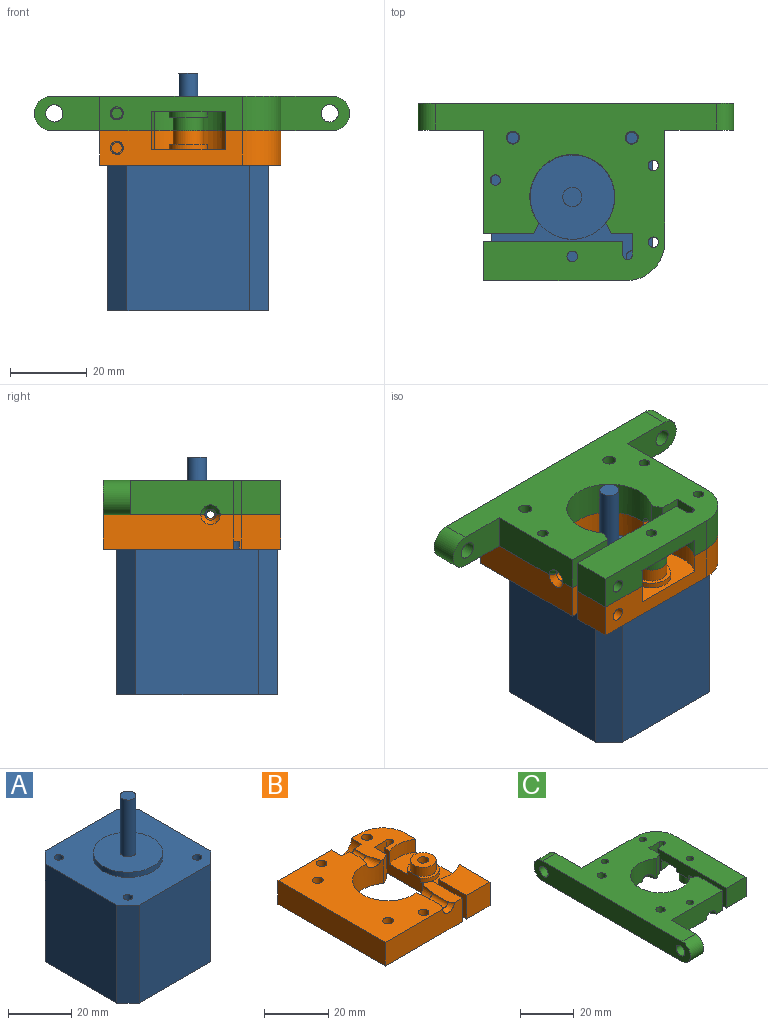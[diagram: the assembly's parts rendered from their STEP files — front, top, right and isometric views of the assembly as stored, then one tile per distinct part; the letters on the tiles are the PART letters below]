
ASSEMBLY  parts=3 mates=1
PART A: 22 faces, bbox 42x42x62 mm
  f0: plane 38x32mm, normal (-1,0,0), area 1216mm2, adj f4,f5,f8,f9
  f1: plane 38x32mm, normal (0,-1,0), area 1216mm2, adj f4,f5,f7,f9
  f2: plane 38x32mm, normal (1,0,0), area 1216mm2, adj f4,f5,f6,f7
  f3: plane 38x32mm, normal (0,1,0), area 1216mm2, adj f4,f5,f6,f8
  f4: plane 42x42mm, normal (0,0,1), area 1305.6mm2, adj f0,f1,f2,f3,f6,f7,f8,f9
  f5: plane 42x42mm, normal (0,0,-1), area 1714mm2, adj f0,f1,f2,f3,f6,f7,f8,f9
  f6: plane 38x5mm, normal (0.71,0.71,0), area 268.7mm2, adj f2,f3,f4,f5
  f7: plane 38x5mm, normal (0.71,-0.71,0), area 268.7mm2, adj f1,f2,f4,f5
  f8: plane 38x5mm, normal (-0.71,0.71,0), area 268.7mm2, adj f0,f3,f4,f5
  f9: plane 38x5mm, normal (-0.71,-0.71,0), area 268.7mm2, adj f0,f1,f4,f5
  f10: cylinder r=11mm len=22mm, axis (0,0,-1), area 138.2mm2, adj f4,f11
  f11: plane 22x22mm, normal (0,0,1), area 360.5mm2, adj f10,f12
  f12: cylinder r=2.5mm len=22mm, axis (0,0,-1), area 345.6mm2, adj f11,f13
  f13: plane 5x5mm, normal (0,0,1), area 19.6mm2, adj f12
  f14: cylinder r=1.5mm len=25mm, axis (0,0,1), area 235.6mm2, adj f4,f15
  f15: plane 3x3mm, normal (0,0,1), area 7.1mm2, adj f14
  f16: cylinder r=1.5mm len=25mm, axis (0,0,1), area 235.6mm2, adj f4,f17
  f17: plane 3x3mm, normal (0,0,1), area 7.1mm2, adj f16
  f18: cylinder r=1.5mm len=25mm, axis (0,0,1), area 235.6mm2, adj f4,f19
  f19: plane 3x3mm, normal (0,0,1), area 7.1mm2, adj f18
  f20: cylinder r=1.5mm len=25mm, axis (0,0,1), area 235.6mm2, adj f4,f21
  f21: plane 3x3mm, normal (0,0,1), area 7.1mm2, adj f20
PART B: 44 faces, bbox 46.2x47.3x9 mm
  f0: plane 47.28x26.93mm, normal (0,0,1), area 962.5mm2, adj f2,f7,f8,f9,f15,f17,f21,f22
  f1: plane 14.38x4.52mm, normal (0,0,1), area 58.8mm2, adj f2,f6,f9,f34,f35,f36,f43
  f2: cylinder r=11.1mm len=22.2mm, axis (0,0,1), area 427.8mm2, adj f0,f1,f3,f20,f29,f33,f34,f42
  f3: plane 17.27x15.32mm, normal (0,0,1), area 163.1mm2, adj f2,f4,f7,f10,f11,f12,f13,f16
  f4: plane 36.35x9mm, normal (-1,0,0), area 219.3mm2, adj f3,f5,f13,f14,f19,f20,f23,f24
  f5: cylinder r=5mm len=10mm, axis (0,0,1), area 37.6mm2, adj f4,f25,f26
  f6: plane 13.04x9mm, normal (1,0,0), area 111.2mm2, adj f1,f9,f20,f38,f43
  f7: plane 36.2x9mm, normal (0,1,0), area 294mm2, adj f0,f3,f8,f20,f30,f37
  f8: plane 47.28x9mm, normal (-1,0,0), area 425.5mm2, adj f0,f7,f9,f20
  f9: plane 33.91x9mm, normal (0,-1,0), area 295mm2, adj f0,f1,f6,f8,f20,f36
  f10: plane 9x5.51mm, normal (1,0,0), area 49.5mm2, adj f3,f11,f20,f42
  f11: plane 9x5.65mm, normal (0,-1,0), area 50.9mm2, adj f3,f10,f12,f20
  f12: cylinder r=1.22mm len=9mm, axis (0,0,-1), area 34.6mm2, adj f3,f11,f13,f20
  f13: plane 9x3.65mm, normal (0,1,0), area 32.9mm2, adj f3,f4,f12,f20
  f14: plane 10.29x9mm, normal (0,-1,0), area 92.6mm2, adj f4,f18,f19,f20
  f15: cylinder r=1.7mm len=9mm, axis (0,0,-1), area 96.1mm2, adj f0,f20
  f16: cylinder r=1.7mm len=9mm, axis (0,0,-1), area 96.1mm2, adj f3,f20
  f17: cylinder r=1.7mm len=9mm, axis (0,0,-1), area 96.1mm2, adj f0,f20
  f18: plane 37.28x9mm, normal (1,0,0), area 230.1mm2, adj f3,f14,f19,f20,f23,f24,f25,f37
  f19: plane 13.53x10.29mm, normal (0,0,1), area 124.8mm2, adj f4,f14,f18,f24
  f20: plane 47.28x46.2mm, normal (0,0,-1), area 1634.4mm2, adj f2,f4,f6,f7,f8,f9,f10,f11
  f21: cylinder r=1.7mm len=9mm, axis (0,0,1), area 96.1mm2, adj f0,f20
  f22: cylinder r=1.7mm len=9mm, axis (0,0,1), area 96.1mm2, adj f0,f20
  f23: cylinder r=11.5mm len=10.29mm, axis (0,0,1), area 53.7mm2, adj f3,f4,f18,f25
  f24: cylinder r=11.5mm len=10.29mm, axis (0,0,1), area 53.7mm2, adj f4,f18,f19,f25
  f25: plane 23x10.29mm, normal (0,0,1), area 152.7mm2, adj f4,f5,f18,f23,f24
  f26: plane 10x9.02mm, normal (0,0,1), area 24.3mm2, adj f4,f5,f27
  f27: cylinder r=4mm len=8mm, axis (0,0,1), area 88mm2, adj f26,f28
  f28: plane 8x8mm, normal (0,0,1), area 41.2mm2, adj f27,f41
  f29: plane 0.6x0.07mm, normal (0,1,0), area 0mm2, adj f2,f3,f33
  f30: cylinder r=4.5mm len=9mm, axis (0,-1,0), area 64.9mm2, adj f0,f3,f7,f31
  f31: plane 9x4.5mm, normal (0,1,0), area 30.2mm2, adj f0,f3,f30,f32
  f32: cylinder r=1mm len=5.13mm, axis (0,-1,0), area 16.1mm2, adj f0,f3,f31,f33
  f33: cone r=1mm half-angle=17.1deg, axis (0,-1,0), area 21.6mm2, adj f0,f2,f3,f29,f32
  f34: cone r=2.55mm half-angle=11deg, axis (0,1,0), area 25.3mm2, adj f0,f1,f2,f35
  f35: cylinder r=1.46mm len=6.91mm, axis (0,-1,0), area 31.7mm2, adj f0,f1,f34,f36
  f36: cone r=1.46mm half-angle=32.9deg, axis (0,-1,0), area 12.6mm2, adj f0,f1,f9,f35
  f37: cylinder r=10mm len=10mm, axis (0,0,-1), area 141.4mm2, adj f3,f7,f18,f20
  f38: cylinder r=1.4mm len=7.71mm, axis (1,0,0), area 67.8mm2, adj f6,f39
  f39: plane 2.8x2.8mm, normal (1,0,0), area 6.2mm2, adj f38
  f40: cylinder r=1.7mm len=10.29mm, axis (1,0,0), area 109.9mm2, adj f4,f18
  f41: cylinder r=1.7mm len=9mm, axis (0,0,1), area 96.1mm2, adj f20,f28
  f42: plane 9x2.71mm, normal (0.44,-0.9,0), area 27.2mm2, adj f2,f3,f10,f20
  f43: plane 9x2.71mm, normal (0.44,0.9,0), area 27.2mm2, adj f1,f2,f6,f20
PART C: 50 faces, bbox 46.2x82.3x9 mm
  f0: plane 73.31x26.93mm, normal (0,0,-1), area 1151.4mm2, adj f2,f8,f9,f10,f16,f17,f21,f22
  f1: plane 14.38x4.52mm, normal (0,0,-1), area 58.8mm2, adj f2,f6,f10,f35,f36,f37,f48
  f2: cylinder r=11.1mm len=22.2mm, axis (0,0,-1), area 427.8mm2, adj f0,f1,f3,f19,f33,f34,f36,f48
  f3: plane 17.27x15.32mm, normal (0,0,-1), area 166.5mm2, adj f2,f4,f5,f7,f8,f11,f12,f13
  f4: plane 36.35x9mm, normal (-1,0,0), area 219.3mm2, adj f3,f13,f14,f18,f19,f23,f24,f25
  f5: plane 37.28x9mm, normal (1,0,0), area 230.1mm2, adj f3,f14,f18,f19,f20,f23,f25,f26
  f6: plane 13.04x9mm, normal (1,0,0), area 111.2mm2, adj f1,f10,f19,f39,f48
  f7: plane 9x5.51mm, normal (1,0,0), area 49.5mm2, adj f3,f11,f19,f49
  f8: plane 29.2x9mm, normal (0,1,0), area 231mm2, adj f0,f3,f19,f20,f32,f43
  f9: plane 82.31x9mm, normal (-1,0,0), area 691.6mm2, adj f0,f19,f44,f45,f46,f47
  f10: plane 26.91x9mm, normal (0,-1,0), area 232mm2, adj f0,f1,f6,f19,f37,f42
  f11: plane 9x5.65mm, normal (0,-1,0), area 50.9mm2, adj f3,f7,f12,f19
  f12: cylinder r=1.22mm len=9mm, axis (0,0,1), area 34.6mm2, adj f3,f11,f13,f19
  f13: plane 9x3.65mm, normal (0,1,0), area 32.9mm2, adj f3,f4,f12,f19
  f14: plane 10.29x9mm, normal (0,-1,0), area 92.6mm2, adj f4,f5,f18,f19
  f15: cylinder r=1.35mm len=9mm, axis (0,0,1), area 76.3mm2, adj f3,f19
  f16: cylinder r=1.35mm len=9mm, axis (0,0,1), area 76.3mm2, adj f0,f19
  f17: cylinder r=1.35mm len=9mm, axis (0,0,1), area 76.3mm2, adj f0,f19
  f18: plane 13.53x10.29mm, normal (0,0,-1), area 124.8mm2, adj f4,f5,f14,f25
  f19: plane 73.31x46.2mm, normal (0,0,1), area 1829.6mm2, adj f2,f4,f5,f6,f7,f8,f9,f10
  f20: cylinder r=10mm len=10mm, axis (0,0,1), area 141.4mm2, adj f3,f5,f8,f19
  f21: cylinder r=1.7mm len=9mm, axis (0,0,-1), area 96.1mm2, adj f0,f19
  f22: cylinder r=1.7mm len=9mm, axis (0,0,-1), area 96.1mm2, adj f0,f19
  f23: cylinder r=11.5mm len=10.29mm, axis (0,0,-1), area 53.7mm2, adj f3,f4,f5,f26
  f24: cylinder r=5mm len=10mm, axis (0,0,-1), area 37.6mm2, adj f4,f26,f28
  f25: cylinder r=11.5mm len=10.29mm, axis (0,0,-1), area 53.7mm2, adj f4,f5,f18,f26
  f26: plane 23x10.29mm, normal (0,0,-1), area 152.7mm2, adj f4,f5,f23,f24,f25
  f27: cylinder r=4mm len=8mm, axis (0,0,-1), area 88mm2, adj f28,f29
  f28: plane 10x9.02mm, normal (0,0,-1), area 24.3mm2, adj f4,f24,f27
  f29: plane 8x8mm, normal (0,0,-1), area 44.1mm2, adj f27,f41
  f30: plane 9x4.5mm, normal (0,1,0), area 30.2mm2, adj f0,f3,f31,f32
  f31: cylinder r=1mm len=5.13mm, axis (0,-1,0), area 16.1mm2, adj f0,f3,f30,f34
  f32: cylinder r=4.5mm len=9mm, axis (0,-1,0), area 64.9mm2, adj f0,f3,f8,f30
  f33: plane 0.6x0.07mm, normal (0,1,0), area 0mm2, adj f2,f3,f34
  f34: cone r=1mm half-angle=17.1deg, axis (0,-1,0), area 21.6mm2, adj f0,f2,f3,f31,f33
  f35: cylinder r=1.46mm len=6.91mm, axis (0,-1,0), area 31.7mm2, adj f0,f1,f36,f37
  f36: cone r=2.55mm half-angle=11deg, axis (0,1,0), area 25.3mm2, adj f0,f1,f2,f35
  f37: cone r=1.46mm half-angle=32.9deg, axis (0,-1,0), area 12.6mm2, adj f0,f1,f10,f35
  f38: plane 2.8x2.8mm, normal (1,0,0), area 6.2mm2, adj f39
  f39: cylinder r=1.4mm len=7.71mm, axis (1,0,0), area 67.8mm2, adj f6,f38
  f40: cylinder r=1.7mm len=10.29mm, axis (1,0,0), area 109.9mm2, adj f4,f5
  f41: cylinder r=1.4mm len=9mm, axis (0,0,-1), area 79.2mm2, adj f19,f29
  f42: plane 17.03x9mm, normal (1,0,0), area 128.7mm2, adj f0,f10,f19,f44,f46
  f43: plane 18x9mm, normal (1,0,0), area 137.4mm2, adj f0,f8,f19,f45,f47
  f44: cylinder r=2.25mm len=7mm, axis (1,0,0), area 99mm2, adj f9,f42
  f45: cylinder r=2.25mm len=7mm, axis (1,0,0), area 99mm2, adj f9,f43
  f46: cylinder r=4.5mm len=9mm, axis (1,0,0), area 99mm2, adj f0,f9,f19,f42
  f47: cylinder r=4.5mm len=9mm, axis (-1,0,0), area 99mm2, adj f0,f9,f19,f43
  f48: plane 9x2.71mm, normal (0.44,0.9,0), area 27.2mm2, adj f1,f2,f6,f19
  f49: plane 9x2.71mm, normal (0.44,-0.9,0), area 27.2mm2, adj f2,f3,f7,f19
PLACE A at identity
PLACE B rot(axis=(0,0,-1),90deg) t=(15.18,21,38)mm
PLACE C rot(axis=(0,0,-1),90deg) t=(15.18,21,38)mm
MATE fastened C.f17 <-> B.f17  axis (0,0,-1) through (0.93,25.43,47)mm
